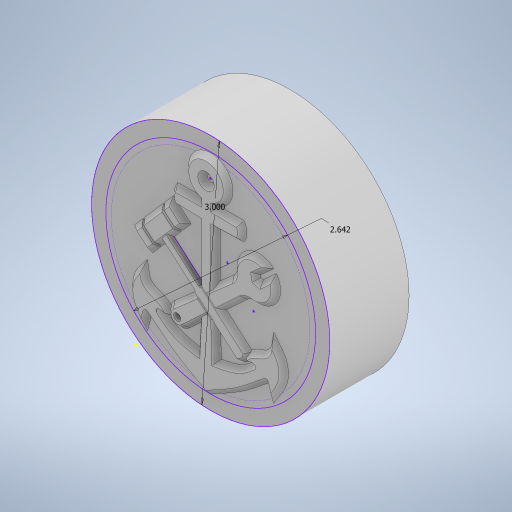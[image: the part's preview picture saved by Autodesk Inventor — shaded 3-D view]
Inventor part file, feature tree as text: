
AUTODESK INVENTOR PART (.ipt)
format: ipt  version: 2024 (Build 280153000, 153)  size: 613,888 bytes
history: native  units: in
note: dims shown in document units (in); Inventor stores cm internally (conversion verified against a paired STEP export)
features: extrude x3, sketch x2, chamfer x1
ambient origin geometry x8: Origin, YZ Plane, XZ Plane, XY Plane, X Axis, Y Axis, Z Axis, Center Point
bodies: Body1 (feature_tree)
feature tree (6):
  sketch  "Sketch4"  dims[d4=0.125in d5=0.0in d7=1.0in d8=0.0in]
  extrude  "Extrusion3"  Depth=1.0in TaperAngle=0.0deg
  extrude  "Extrusion4"  Depth=12.0in TaperAngle=0.0deg
  chamfer  "Chamfer1"  Distance=2.6417in
  extrude  "Extrusion5"  Depth=3.0in
  sketch  "Sketch5"  dims[d9=0.06in d10=0.125in d11=45.0deg d12=12.0in d13=0.0in d14=2.6417in d15=3.0in]
